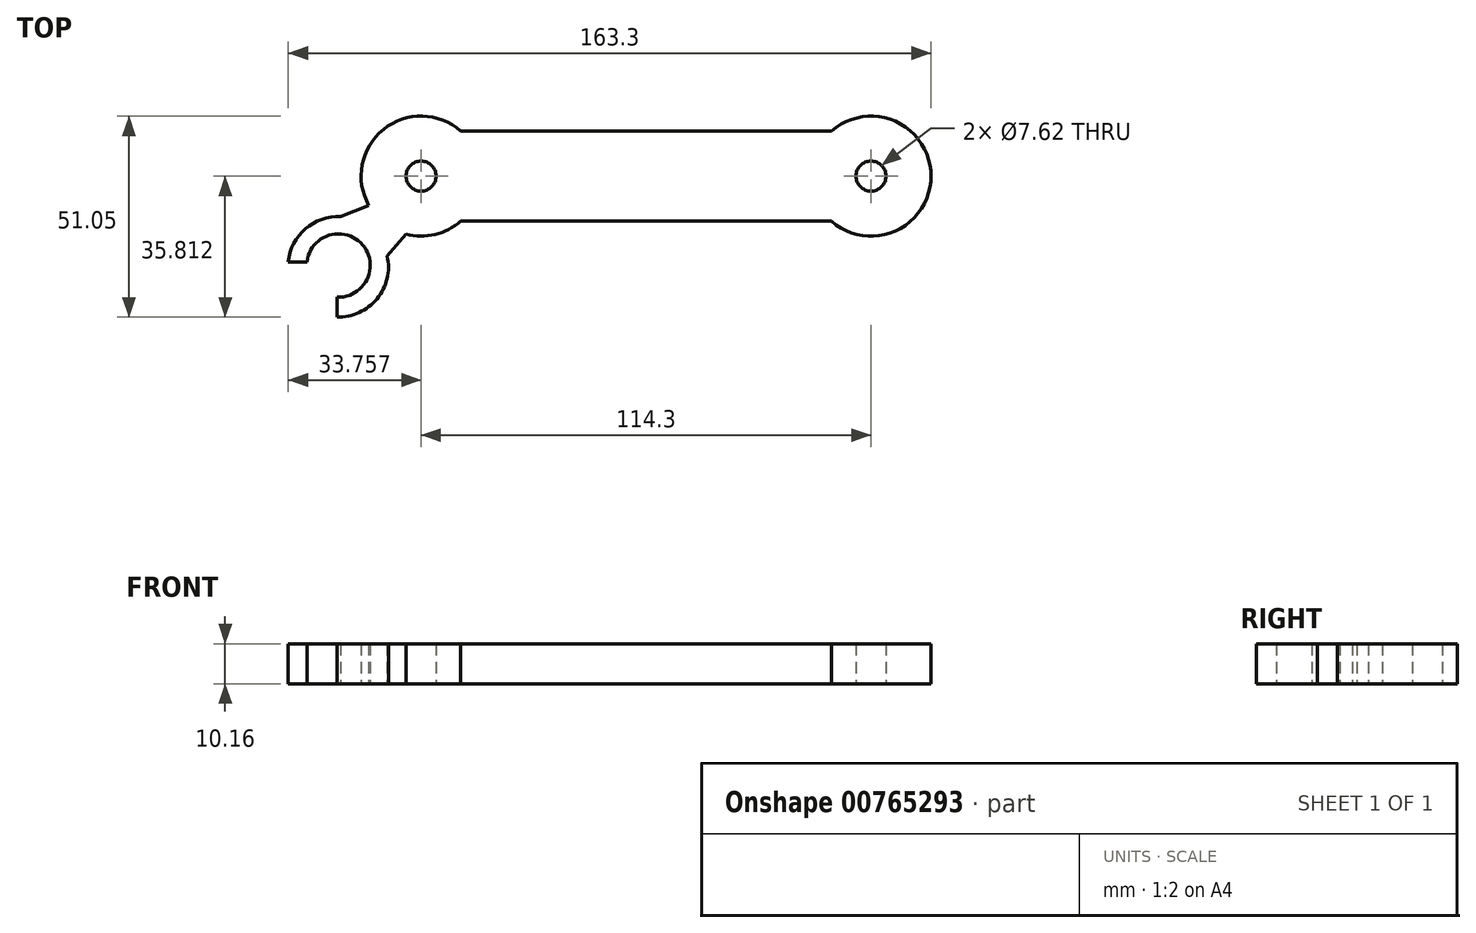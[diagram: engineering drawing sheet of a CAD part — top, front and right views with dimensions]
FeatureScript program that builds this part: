
annotation { "Feature Type Name" : "Feature", "Feature Type Description" : "" }
export const myFeature = defineFeature(function(context is Context, id is Id, definition is map)
    precondition{}
    {
        {
            var Q0;
            Q0=qCreatedBy(makeId("Top.planeOp"),FACE);
            var sketch = newSketch(context, id + "F0", { "sketchPlane" : qUnion([Q0])});
            skLineSegment(sketch, "E0", {"start": v(-60.58, 33.24) * mm, "end": v(53.72, 33.24) * mm});
            skLineSegment(sketch, "E1", {"start": v(53.72, 33.24) * mm, "end": v(53.72, 10.38) * mm});
            skLineSegment(sketch, "E2", {"start": v(53.72, 10.38) * mm, "end": v(-60.58, 10.38) * mm});
            skLineSegment(sketch, "E3", {"start": v(-60.58, 10.38) * mm, "end": v(-60.58, 33.24) * mm});
            skCircle(sketch, "E4", {"center": v(-60.58, 21.81) * mm, "radius": 15.24 * mm});
            skCircle(sketch, "E5", {"center": v(53.72, 21.81) * mm, "radius": 15.24 * mm});
            skCircle(sketch, "E6", {"center": v(53.72, 21.81) * mm, "radius": 3.81 * mm});
            skCircle(sketch, "E7", {"center": v(-60.58, 21.81) * mm, "radius": 3.81 * mm});
            skLineSegment(sketch, "E8", {"start": v(-73.87, 14.36) * mm, "end": v(-80.98, 11.5) * mm});
            skLineSegment(sketch, "E9", {"start": v(-80.98, 11.5) * mm, "end": v(-69.17, 1.5) * mm});
            skLineSegment(sketch, "E10", {"start": v(-69.17, 1.5) * mm, "end": v(-64.45, 7.07) * mm});
            skArc(sketch, "E11", {"start": v(-80.98, 11.5) * mm, "mid": v(-89.9, -10.97) * mm, "end": v(-69.17, 1.5) * mm});
            skCircle(sketch, "E12", {"center": v(-81.58, -0.9) * mm, "radius": 8.06 * mm});
            skLineSegment(sketch, "E13", {"start": v(-89.58, 0) * mm, "end": v(-94.34, 0) * mm});
            skLineSegment(sketch, "E14", {"start": v(-81.93, -8.95) * mm, "end": v(-81.93, -14) * mm});
            skLineSegment(sketch, "E15", {"start": v(-94.34, 0) * mm, "end": v(-81.93, -14) * mm});
            skLineSegment(sketch, "E16", {"start": v(-89.58, 0) * mm, "end": v(-81.93, -8.95) * mm});
            skSolve(sketch);
        }
        {
            var Q0;
            {var subQ0=sQuery(id+"F0.wireOp",EDGE,"E4");var subQ1=sQuery(id+"F0.wireOp",EDGE,"E0");var subQ2=makeQuery(id+"F0.imprint","INTERSECT",VERTEX,{"derivedFrom":[subQ1,subQ0]});Q0=makeQuery(id+"F0.imprint","IMPRINT",FACE,{"disambiguationData":[TD([[makeQuery(id+"F0.imprint","IMPRINT",EDGE,{"disambiguationData":[TD([[subQ2,-1.0]])],"derivedFrom":subQ1}),-1.0]])]});}
            var Q1;
            {var subQ0=sQuery(id+"F0.wireOp",EDGE,"E3");var subQ1=sQuery(id+"F0.wireOp",EDGE,"E0");var subQ2=makeQuery(id+"F0.imprint","INTERSECT",VERTEX,{"derivedFrom":[subQ1,subQ0]});Q1=makeQuery(id+"F0.imprint","IMPRINT",FACE,{"disambiguationData":[TD([[makeQuery(id+"F0.imprint","IMPRINT",EDGE,{"disambiguationData":[TD([[subQ2,-1.0]])],"derivedFrom":subQ1}),-1.0]])]});}
            var Q2;
            {var subQ0=sQuery(id+"F0.wireOp",EDGE,"E3");var subQ1=sQuery(id+"F0.wireOp",EDGE,"E0");var subQ2=makeQuery(id+"F0.imprint","INTERSECT",VERTEX,{"derivedFrom":[subQ1,subQ0]});Q2=makeQuery(id+"F0.imprint","IMPRINT",FACE,{"disambiguationData":[TD([[makeQuery(id+"F0.imprint","IMPRINT",EDGE,{"disambiguationData":[TD([[subQ2,-1.0]])],"derivedFrom":subQ1}),1.0]])]});}
            var Q3;
            {var subQ1=sQuery(id+"F0.wireOp",EDGE,"E1");var subQ7=sQuery(id+"F0.wireOp",EDGE,"E0");var subQ9=makeQuery(id+"F0.imprint","INTERSECT",VERTEX,{"derivedFrom":[subQ7,subQ1]});Q3=makeQuery(id+"F0.imprint","IMPRINT",FACE,{"disambiguationData":[TD([[makeQuery(id+"F0.imprint","IMPRINT",EDGE,{"disambiguationData":[TD([[subQ9,1.0]])],"derivedFrom":subQ7}),-1.0]])]});}
            var Q4;
            {var subQ1=sQuery(id+"F0.wireOp",EDGE,"E1");var subQ5=sQuery(id+"F0.wireOp",EDGE,"E0");var subQ9=makeQuery(id+"F0.imprint","INTERSECT",VERTEX,{"derivedFrom":[subQ5,subQ1]});Q4=makeQuery(id+"F0.imprint","IMPRINT",FACE,{"disambiguationData":[TD([[makeQuery(id+"F0.imprint","IMPRINT",EDGE,{"disambiguationData":[TD([[subQ9,1.0]])],"derivedFrom":subQ5}),1.0]])]});}
            var Q5;
            {var subQ0=sQuery(id+"F0.wireOp",EDGE,"E8");Q5=makeQuery(id+"F0.imprint","IMPRINT",FACE,{"disambiguationData":[TD([[makeQuery(id+"F0.imprint","IMPRINT",EDGE,{"derivedFrom":subQ0}),1.0]])]});}
            var Q6;
            {var subQ5=sQuery(id+"F0.wireOp",EDGE,"E9");Q6=makeQuery(id+"F0.imprint","IMPRINT",FACE,{"disambiguationData":[TD([[makeQuery(id+"F0.imprint","IMPRINT",EDGE,{"derivedFrom":subQ5}),-1.0]])]});}
            extrude(context, id + "F1", {"entities" : qUnion([Q0, Q1, Q2, Q3, Q4, Q5, Q6]), "depth" : 10.16 * mm, "offsetDistance" : 25.4 * mm});
        }
    });
